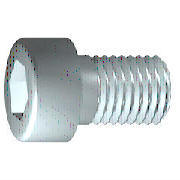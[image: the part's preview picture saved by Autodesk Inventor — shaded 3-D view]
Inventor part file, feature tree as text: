
AUTODESK INVENTOR PART (.ipt)
format: ipt  version: 2020 (Build 240168000, 168)  size: 194,048 bytes
history: native  units: mm (DEFAULTED — no unit token found)
features: sketch x2, extrude x1, plane x1, fillet x1
ambient origin geometry x7: Origin, YZ Plane, XY Plane, X Axis, Y Axis, Z Axis, Center Point
bodies: Solid1 (feature_tree)
feature tree (5):
  extrude  "슬롯"  Depth=18.0mm
  plane  "Work Plane1"
  fillet  "Fillet2"  Radius=0.49086mm
  sketch  "스케치1"
  sketch  "스케치2"
